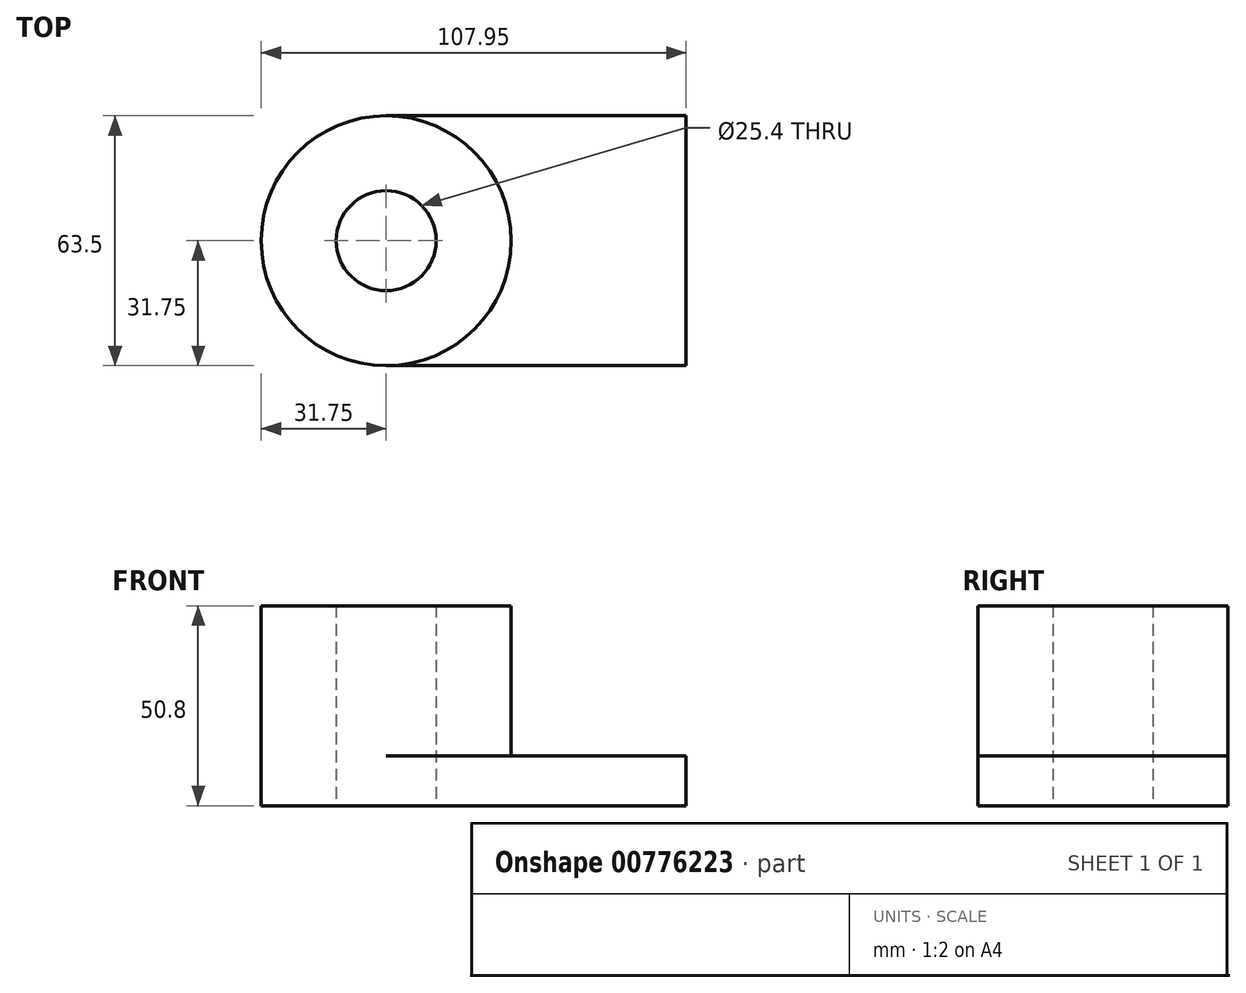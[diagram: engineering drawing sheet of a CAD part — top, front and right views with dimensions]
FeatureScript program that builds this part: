
annotation { "Feature Type Name" : "Feature", "Feature Type Description" : "" }
export const myFeature = defineFeature(function(context is Context, id is Id, definition is map)
    precondition{}
    {
        {
            var Q0;
            Q0=qCreatedBy(makeId("Top.planeOp"),FACE);
            var sketch = newSketch(context, id + "F0", { "sketchPlane" : qUnion([Q0])});
            skLineSegment(sketch, "E0.bottom", {"start": v(38.1, -31.75) * mm, "end": v(-38.1, -31.75) * mm});
            skLineSegment(sketch, "E0.top", {"start": v(38.1, 31.75) * mm, "end": v(-38.1, 31.75) * mm});
            skLineSegment(sketch, "E0.left", {"start": v(38.1, -31.75) * mm, "end": v(38.1, 31.75) * mm});
            skLineSegment(sketch, "E0.right", {"start": v(-38.1, -31.75) * mm, "end": v(-38.1, 31.75) * mm});
            skPoint(sketch, "E0.middle", {"position": v(0, 0) * mm});
            skCircle(sketch, "E1", {"center": v(-38.1, 0) * mm, "radius": 31.75 * mm});
            skCircle(sketch, "E2", {"center": v(-38.1, 0) * mm, "radius": 12.7 * mm});
            skSolve(sketch);
        }
        {
            var Q0;
            Q0 = qSketchRegion(id + "F0", true);
            extrude(context, id + "F1", {"entities" : qUnion([Q0]), "depth" : 12.7 * mm, "offsetDistance" : 25.4 * mm});
        }
        {
            var Q0;
            {var subQ1=sQuery(id+"F0.wireOp",EDGE,"E0.right");var subQ3=sQuery(id+"F0.wireOp",EDGE,"E2");var subQ4=makeQuery(id+"F0.imprint","INTERSECT",VERTEX,{"disambiguationData":[OD(0.0)],"derivedFrom":[subQ1,subQ3]});Q0=makeQuery(id+"F0.imprint","IMPRINT",FACE,{"disambiguationData":[TD([[makeQuery(id+"F0.imprint","IMPRINT",EDGE,{"disambiguationData":[TD([[subQ4,1.0]])],"derivedFrom":subQ3}),-1.0]])]});}
            var Q1;
            {var subQ1=sQuery(id+"F0.wireOp",EDGE,"E0.right");var subQ3=sQuery(id+"F0.wireOp",EDGE,"E2");var subQ4=makeQuery(id+"F0.imprint","INTERSECT",VERTEX,{"disambiguationData":[OD(0.0)],"derivedFrom":[subQ1,subQ3]});Q1=makeQuery(id+"F0.imprint","IMPRINT",FACE,{"disambiguationData":[TD([[makeQuery(id+"F0.imprint","IMPRINT",EDGE,{"disambiguationData":[TD([[subQ4,-1.0]])],"derivedFrom":subQ3}),-1.0]])]});}
            extrude(context, id + "F2", {"entities" : qUnion([Q0, Q1]), "operationType" : NewBodyOperationType.ADD, "depth" : 50.8 * mm, "offsetDistance" : 25.4 * mm});
        }
    });
